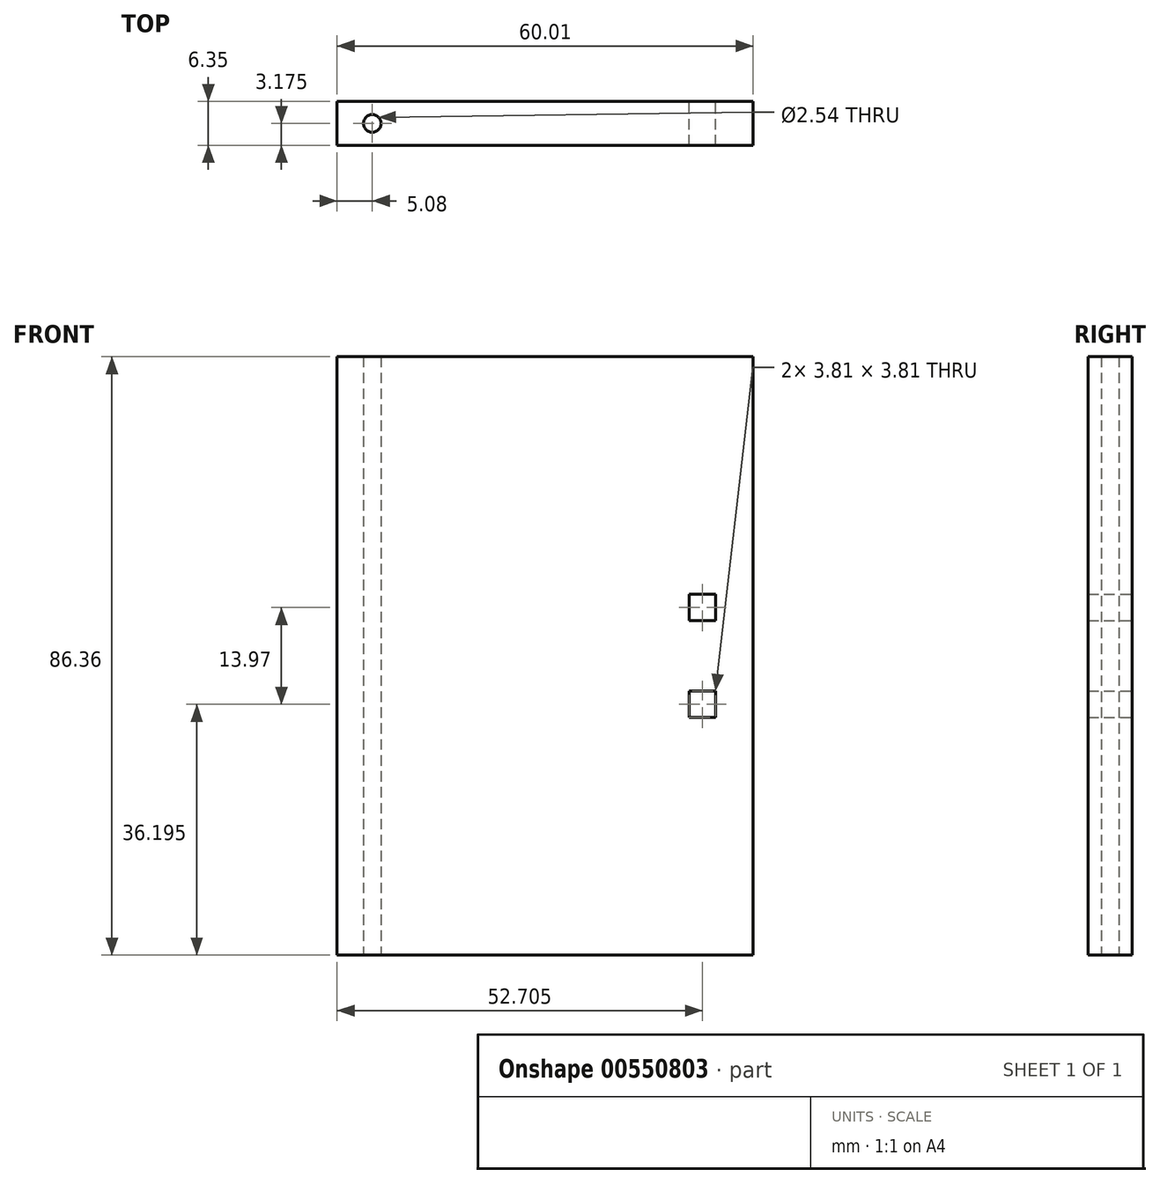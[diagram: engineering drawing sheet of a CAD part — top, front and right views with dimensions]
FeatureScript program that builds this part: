
annotation { "Feature Type Name" : "Feature", "Feature Type Description" : "" }
export const myFeature = defineFeature(function(context is Context, id is Id, definition is map)
    precondition{}
    {
        {
            var Q0;
            Q0=qCreatedBy(makeId("Front.planeOp"),FACE);
            var sketch = newSketch(context, id + "F0", { "sketchPlane" : qUnion([Q0])});
            skLineSegment(sketch, "E0.bottom", {"start": v(0, 0) * mm, "end": v(60, 0) * mm});
            skLineSegment(sketch, "E0.top", {"start": v(0, 86.36) * mm, "end": v(60, 86.36) * mm});
            skLineSegment(sketch, "E0.left", {"start": v(0, 0) * mm, "end": v(0, 86.36) * mm});
            skLineSegment(sketch, "E0.right", {"start": v(60, 0) * mm, "end": v(60, 86.36) * mm});
            skLineSegment(sketch, "E1", {"start": v(0, 43.18) * mm, "end": v(60, 43.18) * mm, "construction": true});
            skLineSegment(sketch, "E2.bottom", {"start": v(50.8, 38.1) * mm, "end": v(54.6, 38.1) * mm});
            skLineSegment(sketch, "E2.top", {"start": v(50.8, 34.3) * mm, "end": v(54.6, 34.3) * mm});
            skLineSegment(sketch, "E2.left", {"start": v(50.8, 38.1) * mm, "end": v(50.8, 34.3) * mm});
            skLineSegment(sketch, "E2.right", {"start": v(54.6, 38.1) * mm, "end": v(54.6, 34.3) * mm});
            skLineSegment(sketch, "E3.bottom", {"start": v(50.8, 48.26) * mm, "end": v(54.6, 48.26) * mm});
            skLineSegment(sketch, "E3.top", {"start": v(50.8, 52.07) * mm, "end": v(54.6, 52.07) * mm});
            skLineSegment(sketch, "E3.left", {"start": v(50.8, 48.26) * mm, "end": v(50.8, 52.07) * mm});
            skLineSegment(sketch, "E3.right", {"start": v(54.6, 48.26) * mm, "end": v(54.6, 52.07) * mm});
            skSolve(sketch);
        }
        {
            var Q0;
            Q0=makeQuery(id+"F0.imprint","IMPRINT",FACE,{"disambiguationData":[TD([[makeQuery(id+"F0.imprint","IMPRINT",EDGE,{"derivedFrom":sQuery(id+"F0.wireOp",EDGE,"E0.bottom")}),1.0]])]});
            var Q1;
            Q1=sQuery(id+"F0.wireOp",EDGE,"E0.bottom");
            var Q2;
            Q2=sQuery(id+"F0.wireOp",EDGE,"E0.right");
            var Q3;
            Q3=sQuery(id+"F0.wireOp",EDGE,"E0.left");
            var Q4;
            Q4=sQuery(id+"F0.wireOp",EDGE,"E0.top");
            var Q5;
            Q5=sQuery(id+"F0.wireOp",EDGE,"3q6ImQ98-CW6B-MR4E-VbdS-baekhzimJ0Ja");
            var Q6;
            Q6=sQuery(id+"F0.wireOp",EDGE,"rFB2NzFO-SasR-8dDC-dUop-9rWW89sOPrpC");
            extrude(context, id + "F1", {"entities" : qUnion([Q0]), "surfaceEntities" : qUnion([Q1, Q2, Q3, Q4, Q5, Q6]), "depth" : 6.35 * mm, "offsetDistance" : 25.4 * mm});
        }
        {
            var Q0;
            Q0=qCreatedBy(makeId("Top.planeOp"),FACE);
            var sketch = newSketch(context, id + "F2", { "sketchPlane" : qUnion([Q0])});
            skCircle(sketch, "E4", {"center": v(5.08, -3.18) * mm, "radius": 1.27 * mm});
            skSolve(sketch);
        }
        {
            var Q0;
            Q0 = qSketchRegion(id + "F2", true);
            extrude(context, id + "F3", {"entities" : qUnion([Q0]), "operationType" : NewBodyOperationType.REMOVE, "endBound" : BoundingType.THROUGH_ALL, "depth" : 25.4 * mm, "offsetDistance" : 25.4 * mm});
        }
    });
